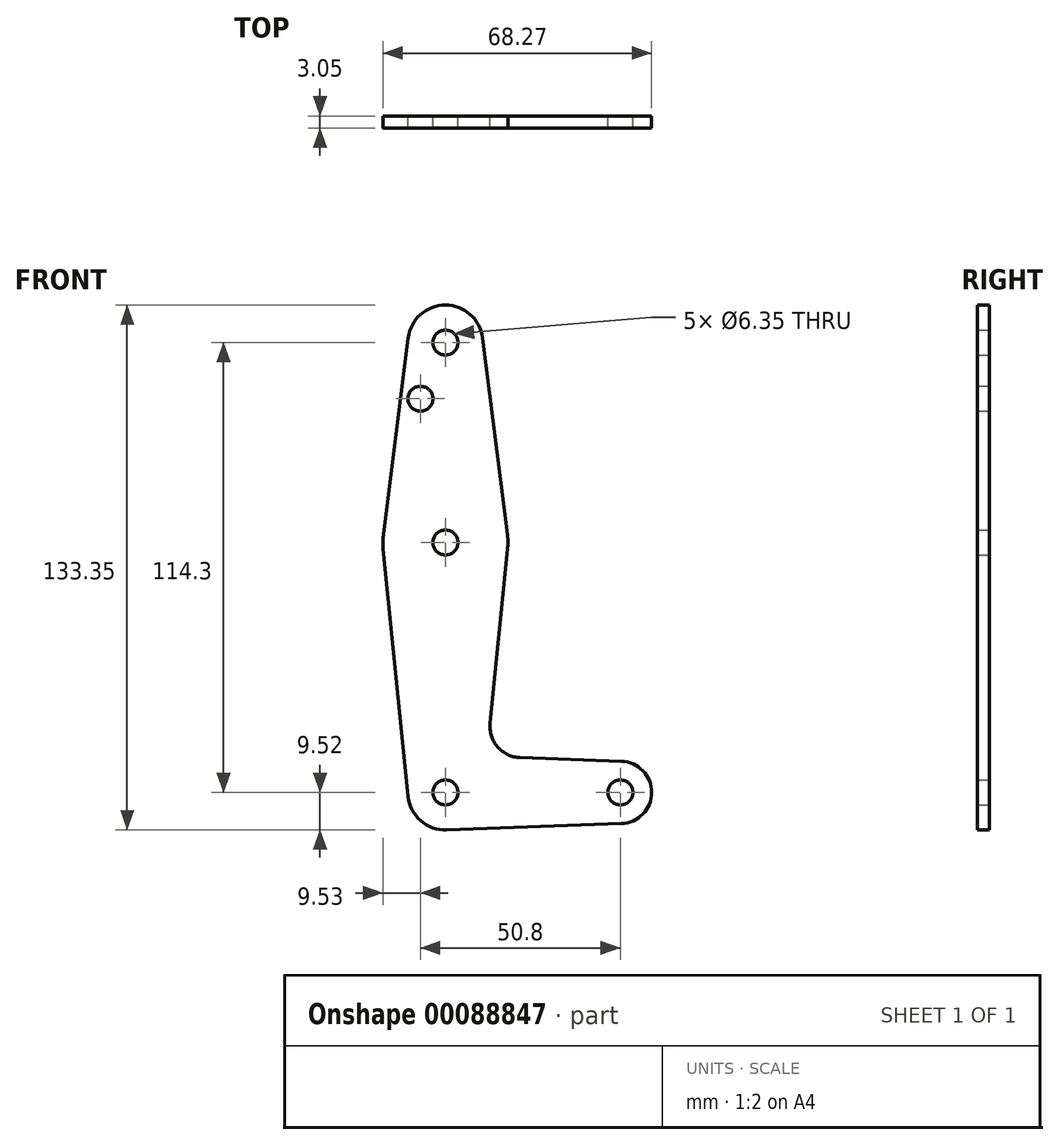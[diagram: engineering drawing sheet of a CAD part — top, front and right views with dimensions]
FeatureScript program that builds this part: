
annotation { "Feature Type Name" : "Feature", "Feature Type Description" : "" }
export const myFeature = defineFeature(function(context is Context, id is Id, definition is map)
    precondition{}
    {
        {
            var Q0;
            Q0=qCreatedBy(makeId("Front.planeOp"),FACE);
            var sketch = newSketch(context, id + "F0", { "sketchPlane" : qUnion([Q0])});
            skCircle(sketch, "E0", {"center": v(0, 114.3) * mm, "radius": 9.53 * mm});
            skCircle(sketch, "E1", {"center": v(0, 63.5) * mm, "radius": 15.88 * mm});
            skCircle(sketch, "E2", {"center": v(0, 0) * mm, "radius": 9.53 * mm});
            skCircle(sketch, "E3", {"center": v(44.45, 0) * mm, "radius": 7.94 * mm});
            skLineSegment(sketch, "E4", {"start": v(0, 114.3) * mm, "end": v(0, 63.5) * mm, "construction": true});
            skLineSegment(sketch, "E5", {"start": v(0, 63.5) * mm, "end": v(0, 0) * mm, "construction": true});
            skLineSegment(sketch, "E6", {"start": v(0, 0) * mm, "end": v(44.45, 0) * mm, "construction": true});
            skLineSegment(sketch, "E7", {"start": v(-9.45, 115.5) * mm, "end": v(-15.75, 65.48) * mm});
            skLineSegment(sketch, "E8", {"start": v(9.45, 115.5) * mm, "end": v(15.75, 65.48) * mm});
            skPoint(sketch, "E9.newPointB", {"position": v(18.85, 0) * mm});
            skLineSegment(sketch, "E10", {"start": v(0, 100.03) * mm, "end": v(0, 63.5) * mm, "construction": true});
            skCircle(sketch, "E11", {"center": v(0, 114.3) * mm, "radius": 3.18 * mm});
            skLineSegment(sketch, "E12", {"start": v(0.34, -9.52) * mm, "end": v(44.73, -7.93) * mm});
            skLineSegment(sketch, "E13", {"start": v(18.97, 8.85) * mm, "end": v(44.73, 7.93) * mm});
            skLineSegment(sketch, "E14", {"start": v(11.34, 17.6) * mm, "end": v(15.8, 61.91) * mm});
            skArc(sketch, "E15.filletArc", {"start": v(11.34, 17.6) * mm, "mid": v(13.26, 11.57) * mm, "end": v(18.97, 8.85) * mm});
            skCircle(sketch, "E16", {"center": v(-6.35, 100.03) * mm, "radius": 3.18 * mm});
            skCircle(sketch, "E17", {"center": v(44.45, 0) * mm, "radius": 3.18 * mm});
            skCircle(sketch, "E18", {"center": v(0, 0) * mm, "radius": 3.18 * mm});
            skCircle(sketch, "E19", {"center": v(0, 63.5) * mm, "radius": 3.18 * mm});
            skLineSegment(sketch, "E20", {"start": v(-15.8, 61.91) * mm, "end": v(-9.48, -0.95) * mm});
            skSolve(sketch);
        }
        {
            var Q0;
            Q0 = qSketchRegion(id + "F0", true);
            extrude(context, id + "F1", {"entities" : qUnion([Q0]), "depth" : 3.05 * mm});
        }
    });
